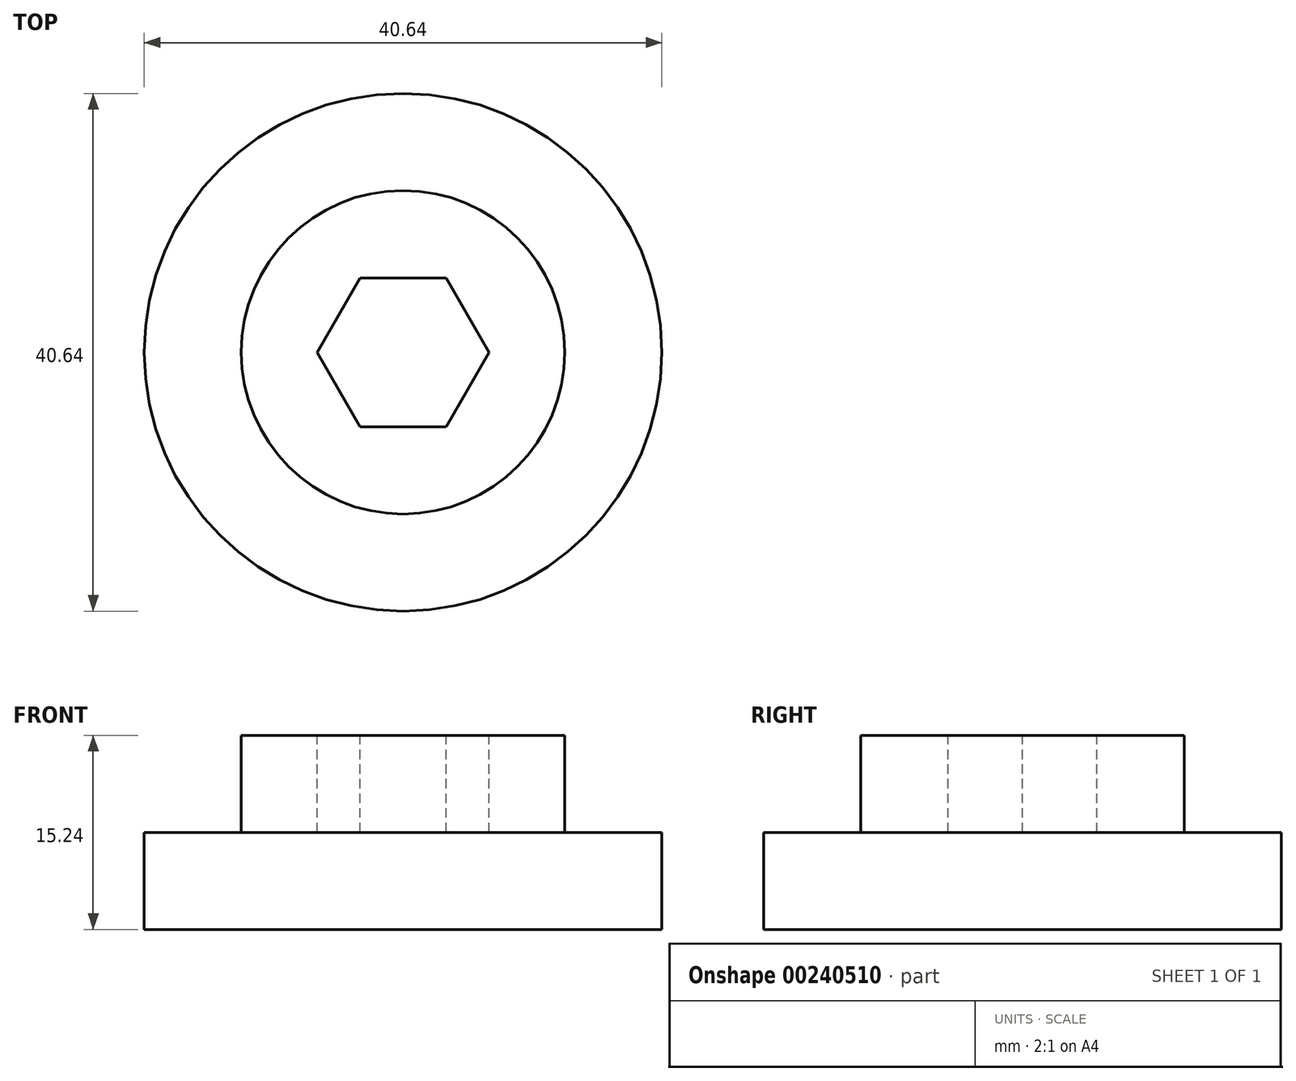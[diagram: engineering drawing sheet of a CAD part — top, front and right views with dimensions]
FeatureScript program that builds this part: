
annotation { "Feature Type Name" : "Feature", "Feature Type Description" : "" }
export const myFeature = defineFeature(function(context is Context, id is Id, definition is map)
    precondition{}
    {
        {
            var Q0;
            Q0=qCreatedBy(makeId("Top.planeOp"),FACE);
            var sketch = newSketch(context, id + "F0", { "sketchPlane" : qUnion([Q0])});
            skCircle(sketch, "E0", {"center": v(0, 0) * mm, "radius": 20.32 * mm});
            skSolve(sketch);
        }
        {
            var Q0;
            Q0 = qSketchRegion(id + "F0", true);
            extrude(context, id + "F1", {"entities" : qUnion([Q0]), "depth" : 7.62 * mm});
        }
        {
            var Q0;
            Q0=makeQuery(id+"F1.opExtrude","CAP_FACE",FACE,{"disambiguationData":[OSD([sQuery(id+"F0.wireOp",EDGE,"E0")])],"isStart":false});
            var sketch = newSketch(context, id + "F2", { "sketchPlane" : qUnion([Q0])});
            skCircle(sketch, "E1", {"center": v(0, 0) * mm, "radius": 12.7 * mm});
            skSolve(sketch);
        }
        {
            var Q0;
            Q0 = qSketchRegion(id + "F2", true);
            extrude(context, id + "F3", {"entities" : qUnion([Q0]), "operationType" : NewBodyOperationType.ADD, "depth" : 7.62 * mm});
        }
        {
            var Q0;
            Q0=makeQuery(id+"F3.opExtrude","CAP_FACE",FACE,{"disambiguationData":[OSD([sQuery(id+"F2.wireOp",EDGE,"E1")])],"isStart":false});
            var sketch = newSketch(context, id + "F4", { "sketchPlane" : qUnion([Q0])});
            skCircle(sketch, "E2.cCircle", {"center": v(0, 0) * mm, "radius": 5.84 * mm, "construction": true});
            skLineSegment(sketch, "E2.0", {"start": v(-3.37, 5.84) * mm, "end": v(3.37, 5.84) * mm});
            skLineSegment(sketch, "E2.1", {"start": v(3.37, 5.84) * mm, "end": v(6.75, 0) * mm});
            skLineSegment(sketch, "E2.2", {"start": v(6.75, 0) * mm, "end": v(3.37, -5.84) * mm});
            skLineSegment(sketch, "E2.3", {"start": v(3.37, -5.84) * mm, "end": v(-3.37, -5.84) * mm});
            skLineSegment(sketch, "E2.4", {"start": v(-3.37, -5.84) * mm, "end": v(-6.75, 0) * mm});
            skLineSegment(sketch, "E2.5", {"start": v(-6.75, 0) * mm, "end": v(-3.37, 5.84) * mm});
            skPoint(sketch, "E2.0.midPoint", {"position": v(0, 5.84) * mm});
            skSolve(sketch);
        }
        {
            var Q0;
            Q0 = qSketchRegion(id + "F4", true);
            extrude(context, id + "F5", {"entities" : qUnion([Q0]), "operationType" : NewBodyOperationType.REMOVE, "oppositeDirection" : true, "depth" : 7.62 * mm});
        }
    });
